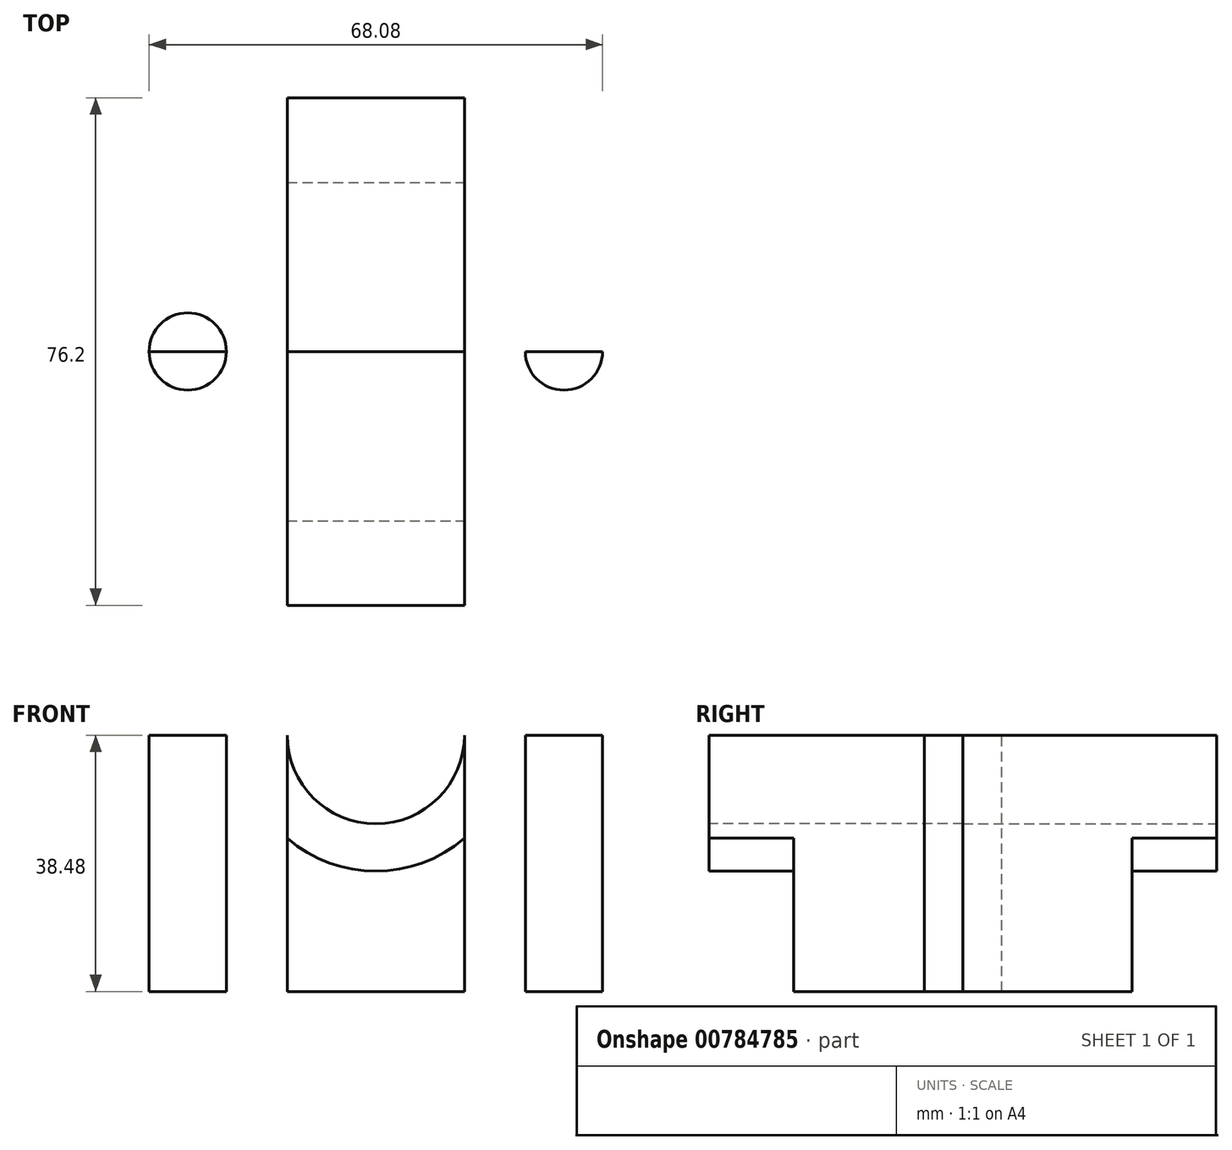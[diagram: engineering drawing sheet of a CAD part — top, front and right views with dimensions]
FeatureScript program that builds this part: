
annotation { "Feature Type Name" : "Feature", "Feature Type Description" : "" }
export const myFeature = defineFeature(function(context is Context, id is Id, definition is map)
    precondition{}
    {
        {
            var Q0;
            Q0=qCreatedBy(makeId("Front.planeOp"),FACE);
            var sketch = newSketch(context, id + "F0", { "sketchPlane" : qUnion([Q0])});
            skLineSegment(sketch, "E0", {"start": v(-37.87, 0) * mm, "end": v(-37.87, 38.48) * mm});
            skLineSegment(sketch, "E1", {"start": v(-37.87, 38.48) * mm, "end": v(-20.4, 38.48) * mm});
            skLineSegment(sketch, "E2", {"start": v(-37.87, 0) * mm, "end": v(0, 0) * mm});
            skArc(sketch, "E3", {"start": v(-20.4, 38.48) * mm, "mid": v(-14.43, 24.05) * mm, "end": v(0, 18.07) * mm});
            skLineSegment(sketch, "E4", {"start": v(0, 18.07) * mm, "end": v(0, 0) * mm});
            skArc(sketch, "E5", {"start": v(-13.3, 38.48) * mm, "mid": v(-9.4, 29.08) * mm, "end": v(0, 25.18) * mm});
            skLineSegment(sketch, "E6", {"start": v(-13.3, 38.48) * mm, "end": v(-20.4, 38.48) * mm});
            skLineSegment(sketch, "E7", {"start": v(0, 25.18) * mm, "end": v(0, 18.07) * mm});
            skSolve(sketch);
        }
        {
            var Q0;
            Q0 = qSketchRegion(id + "F0", true);
            extrude(context, id + "F1", {"entities" : qUnion([Q0]), "oppositeDirection" : true, "depth" : 25.4 * mm, "offsetDistance" : 25.4 * mm});
        }
        {
            var Q0;
            Q0=makeQuery(id+"F0.imprint","IMPRINT",FACE,{"disambiguationData":[TD([[makeQuery(id+"F0.imprint","IMPRINT",EDGE,{"derivedFrom":sQuery(id+"F0.wireOp",EDGE,"E3")}),1.0]])]});
            extrude(context, id + "F2", {"entities" : qUnion([Q0]), "operationType" : NewBodyOperationType.ADD, "depth" : 12.7 * mm, "offsetDistance" : 25.4 * mm});
        }
        {
            var Q0;
            {var subQ0=sQuery(id+"F0.wireOp",EDGE,"E6");Q0=makeQuery(id+"F2.boolean.opBoolean","MERGE",FACE,{"derivedFrom":[makeQuery(id+"F1.opExtrude","SWEPT_FACE",FACE,{"disambiguationData":[OSD([sQuery(id+"F0.wireOp",EDGE,"E1"),subQ0])]}),makeQuery(id+"F2.opExtrude","SWEPT_FACE",FACE,{"disambiguationData":[OSD([subQ0])]})]});}
            var sketch = newSketch(context, id + "F3", { "sketchPlane" : qUnion([Q0])});
            skArc(sketch, "E8", {"start": v(-22.44, 25.4) * mm, "mid": v(-28.24, 19.6) * mm, "end": v(-34.04, 25.4) * mm});
            skSolve(sketch);
        }
        {
            var Q0;
            {var subQ0=sQuery(id+"F3.wireOp",EDGE,"E8");Q0=makeQuery(id+"F3.imprint","IMPRINT",FACE,{"disambiguationData":[TD([[makeQuery(id+"F3.imprint","IMPRINT",EDGE,{"derivedFrom":subQ0}),-1.0]])]});}
            extrude(context, id + "F4", {"entities" : qUnion([Q0]), "operationType" : NewBodyOperationType.REMOVE, "oppositeDirection" : true, "depth" : 254 * mm, "offsetDistance" : 25.4 * mm});
        }
        {
            var Q0;
            Q0=makeQuery(id+"F1.opExtrude","SWEPT_BODY",BODY,{"disambiguationData":[OSD([sQuery(id+"F0.wireOp",EDGE,"E0"),sQuery(id+"F0.wireOp",EDGE,"E1"),sQuery(id+"F0.wireOp",EDGE,"E2"),sQuery(id+"F0.wireOp",EDGE,"E4"),sQuery(id+"F0.wireOp",EDGE,"E5"),sQuery(id+"F0.wireOp",EDGE,"E6"),sQuery(id+"F0.wireOp",EDGE,"E7")])]});
            var Q1;
            {var subQ0=sQuery(id+"F0.wireOp",EDGE,"E7");Q1=makeQuery(id+"F2.boolean.opBoolean","MERGE",FACE,{"derivedFrom":[makeQuery(id+"F1.opExtrude","SWEPT_FACE",FACE,{"disambiguationData":[OSD([sQuery(id+"F0.wireOp",EDGE,"E4"),subQ0])]}),makeQuery(id+"F2.opExtrude","SWEPT_FACE",FACE,{"disambiguationData":[OSD([subQ0])]})]});}
            mirror(context, id + "F5", {"operationType" : NewBodyOperationType.ADD, "entities" : qUnion([Q0]), "mirrorPlane" : qUnion([Q1])});
        }
        {
            var Q0;
            Q0=makeQuery(id+"F1.opExtrude","SWEPT_BODY",BODY,{"disambiguationData":[OSD([sQuery(id+"F0.wireOp",EDGE,"E0"),sQuery(id+"F0.wireOp",EDGE,"E1"),sQuery(id+"F0.wireOp",EDGE,"E2"),sQuery(id+"F0.wireOp",EDGE,"E4"),sQuery(id+"F0.wireOp",EDGE,"E5"),sQuery(id+"F0.wireOp",EDGE,"E6"),sQuery(id+"F0.wireOp",EDGE,"E7")])]});
            var Q1;
            {var subQ0=sQuery(id+"F0.wireOp",EDGE,"E5");var subQ1=sQuery(id+"F0.wireOp",EDGE,"E7");var subQ2=sQuery(id+"F0.wireOp",EDGE,"E4");var subQ3=sQuery(id+"F0.wireOp",EDGE,"E2");var subQ4=sQuery(id+"F0.wireOp",EDGE,"E6");var subQ5=sQuery(id+"F0.wireOp",EDGE,"E1");var subQ6=makeQuery(id+"F4.boolean.opBoolean","SPLIT",FACE,{"disambiguationData":[TD([makeQuery(id+"F1.opExtrude","SWEPT_FACE",FACE,{"disambiguationData":[OSD([subQ0])]})])],"derivedFrom":makeQuery(id+"F1.opExtrude","CAP_FACE",FACE,{"disambiguationData":[OSD([sQuery(id+"F0.wireOp",EDGE,"E0"),subQ5,subQ3,subQ2,subQ0,subQ4,subQ1])],"isStart":false})});Q1=makeQuery(id+"F5.boolean.opBoolean","MERGE",FACE,{"derivedFrom":[subQ6,makeQuery(id+"F5.opPattern","COPY",FACE,{"derivedFrom":subQ6,"instanceName":"1"})]});}
            mirror(context, id + "F6", {"operationType" : NewBodyOperationType.ADD, "entities" : qUnion([Q0]), "mirrorPlane" : qUnion([Q1])});
        }
    });
